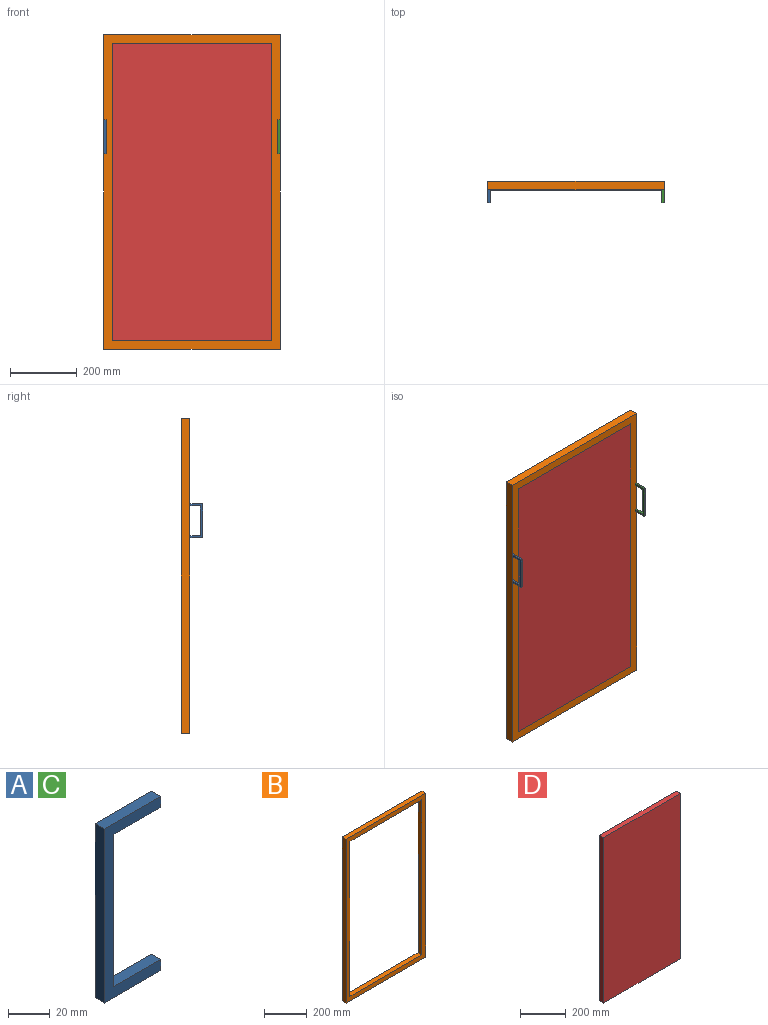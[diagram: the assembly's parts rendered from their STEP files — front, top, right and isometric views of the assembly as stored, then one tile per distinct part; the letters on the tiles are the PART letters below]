
ASSEMBLY  parts=4 mates=4
PART A: 10 faces, bbox 38.1x6.4x101.6 mm
  f0: plane 38.1x6.35mm, normal (0,0,-1), area 241.9mm2, adj f1,f7,f8,f9
  f1: plane 6.35x6.35mm, normal (1,0,0), area 40.3mm2, adj f0,f2,f8,f9
  f2: plane 31.75x6.35mm, normal (0,0,1), area 201.6mm2, adj f1,f3,f8,f9
  f3: plane 88.9x6.35mm, normal (1,0,0), area 564.5mm2, adj f2,f4,f8,f9
  f4: plane 31.75x6.35mm, normal (0,0,-1), area 201.6mm2, adj f3,f5,f8,f9
  f5: plane 6.35x6.35mm, normal (1,0,0), area 40.3mm2, adj f4,f6,f8,f9
  f6: plane 38.1x6.35mm, normal (0,0,1), area 241.9mm2, adj f5,f7,f8,f9
  f7: plane 101.6x6.35mm, normal (-1,0,0), area 645.2mm2, adj f0,f6,f8,f9
  f8: plane 101.6x38.1mm, normal (0,-1,0), area 1048.4mm2, adj f0,f1,f2,f3,f4,f5,f6,f7
  f9: plane 101.6x38.1mm, normal (0,1,0), area 1048.4mm2, adj f0,f1,f2,f3,f4,f5,f6,f7
PART B: 10 faces, bbox 527.1x25.4x939.8 mm
  f0: plane 527.05x25.4mm, normal (0,0,1), area 13387.1mm2, adj f1,f7,f8,f9
  f1: plane 939.8x25.4mm, normal (-1,0,0), area 23870.9mm2, adj f0,f2,f8,f9
  f2: plane 527.05x25.4mm, normal (0,0,-1), area 13387.1mm2, adj f1,f7,f8,f9
  f3: plane 889x25.4mm, normal (-1,0,0), area 22580.6mm2, adj f4,f6,f8,f9
  f4: plane 476.25x25.4mm, normal (0,0,1), area 12096.8mm2, adj f3,f5,f8,f9
  f5: plane 889x25.4mm, normal (1,0,0), area 22580.6mm2, adj f4,f6,f8,f9
  f6: plane 476.25x25.4mm, normal (0,0,-1), area 12096.8mm2, adj f3,f5,f8,f9
  f7: plane 939.8x25.4mm, normal (1,0,0), area 23870.9mm2, adj f0,f2,f8,f9
  f8: plane 939.8x527.05mm, normal (0,-1,0), area 71935.3mm2, adj f0,f1,f2,f3,f4,f5,f6,f7
  f9: plane 939.8x527.05mm, normal (0,1,0), area 71935.3mm2, adj f0,f1,f2,f3,f4,f5,f6,f7
PART C: same geometry as A
PART D: 6 faces, bbox 476.3x25.4x889 mm
  f0: plane 476.25x25.4mm, normal (0,0,1), area 12096.8mm2, adj f1,f3,f4,f5
  f1: plane 889x25.4mm, normal (-1,0,0), area 22580.6mm2, adj f0,f2,f4,f5
  f2: plane 476.25x25.4mm, normal (0,0,-1), area 12096.7mm2, adj f1,f3,f4,f5
  f3: plane 889x25.4mm, normal (1,0,0), area 22580.6mm2, adj f0,f2,f4,f5
  f4: plane 889x476.25mm, normal (0,-1,0), area 423386.2mm2, adj f0,f1,f2,f3
  f5: plane 889x476.25mm, normal (0,1,0), area 423386.2mm2, adj f0,f1,f2,f3
PLACE A rot(axis=(0,0,1),90deg) t=(-303.1,115.07,397.38)mm
PLACE B t=(-303.1,178.57,-186.82)mm
PLACE C rot(axis=(0,0,1),90deg) t=(217.6,115.07,397.38)mm
PLACE D t=(-277.7,178.57,-161.42)mm
MATE fastened D.f4 <-> B.f8  axis (0,-1,0) through (-277.7,153.17,727.58)mm
MATE fastened A.f5 <-> B.f8  axis (0,1,0) through (-303.1,153.17,498.98)mm
MATE fastened C.f5 <-> B.f8  axis (0,1,0) through (223.95,153.17,498.98)mm
MATE fastened B.f8 <-> B.f6  axis (0,-1,0) through (-39.58,153.17,283.08)mm
